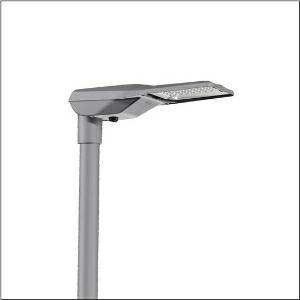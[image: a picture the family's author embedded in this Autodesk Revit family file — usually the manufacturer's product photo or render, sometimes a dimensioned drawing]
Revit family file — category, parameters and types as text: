
# Revit family: streetlight_sl_21_mini___p0_8ab_5xe2r33r08jb_3d56
name_source: partatom
category: Lighting Fixtures
units: mm (PartAtom-declared; Revit-internal decimal feet)

## family parameters
Cut with Voids When Loaded = No
Host = Face
Light Source = No
Part Type = Normal
Room Calculation Point = No
Round Connector Dimension = Use Diameter
Shared = No

## types (1)
- --- (1 x LED, 11230 lm, 88.6 W, 3000K)
    Apparent Load = 89 VA
    CIE Flux Codes = 39 72 97 100 100
    Color Rendering = 70
    Color Temperature = 3000K
    Default Elevation = 1800 mm
    Description = Streetlight SL 21 mini, mast luminaire, primary light control with lens, of PMMA, primary optical cover: cover, of toughened safety glass, transparent, light distribution: P0.8aB, light emission: direct distribution, primary light characteristic: asymmetric, installation type: post-top, side-entry, LED, High Power LED, rated luminous flux: 11.230lm, luminous efficacy: 127lm/W, light colour: 730, colour temperature: 3000K, control gear: D4i, control: pre-setting: logarithmic dimming characteristic, flexible luminous flux parameterisation, time-dependent luminous flux control, constant luminous flux control, overheat protection, mains connection: 220..240V, AC, 50/60Hz, start of lifetime: 89W, end of service life: 92W, reduction: 41W, luminaire housing, of diecast aluminium, powder-coated, SITECO metallic grey (DB 702S), corrosivity category C5 high according to DIN EN ISO 12944, multi-level sealing system, sealing non-destructively replaceable, inclination adjustable: 0°, 5°, 10°, 15°, please order mast flange separately, length: 628mm, width: 235mm, height: 110mm, mast flange for spigot size: 42mm (side-entry): 5XC10008XM4, 60/48mm (side-entry/post-top): 5XC10108XM2, 76/60mm (side-entry/post-top): 5XC10108XM1, mounting height: 4..8m, Smart Interface below, protection rating (complete): IP66, insulation class (complete): insulation class II (safety insulation), certification: CE, ENEC, ENEC+, VDE, impact resistance: IK10, permissible operating ambient temperature for outdoor applications: -40..+50°C, standard-compliant lighting for roads and squares, packaging unit: 1 piece

Light Distribution: P0.8aB
    Height = 110 mm
    Lamp = 1 x LED
    Lamp Light Flux = 11230 lm
    Lamp Power = 88.6 W
    Lamp count = 1
    Length = 625 mm
    Luminous efficacy = 127 lm/W
    Manufacturer = Siteco
    ModVariant = No
    Model = 5XE2R33R08JB
    Number of Poles = 1
    OnlyDefault = Yes
    Power Factor = 1
    Product Name = Streetlight SL 21 mini | P0.8aB
    Product group = mast luminaire | pylon top
    ProductGroupID = 6100
    Protection Class = Protection class II
    Protection Degree = IP 66
    RLX_Detail_Level = 1
    RLX_Emergency_Light_Flux = 0 lm
    RLX_Emergency_Type = 0
    RLX_Emergency_Type_DB = No
    RlxData = <blob elided: 26009 chars, md5=1685c5b4>
    Socket = socket
    Standby Power = 0 W
    System Light Flux = 11230 lm
    System Power = 89 W
    Type Comments = factory setting: luminous flux: 100 % | dim-lin: 254 | 915 mA
    Type Image = l_1003516.jpg
    URL = http://relux.com
    VarID = @adj_033001
    Voltage = 0 V
    Weight = 0.00 kg
    Width = 234 mm

## geometry (parser evidence)
native form markers: Blend x4, Sweep x9
no freeform markers — native parametric forms only
